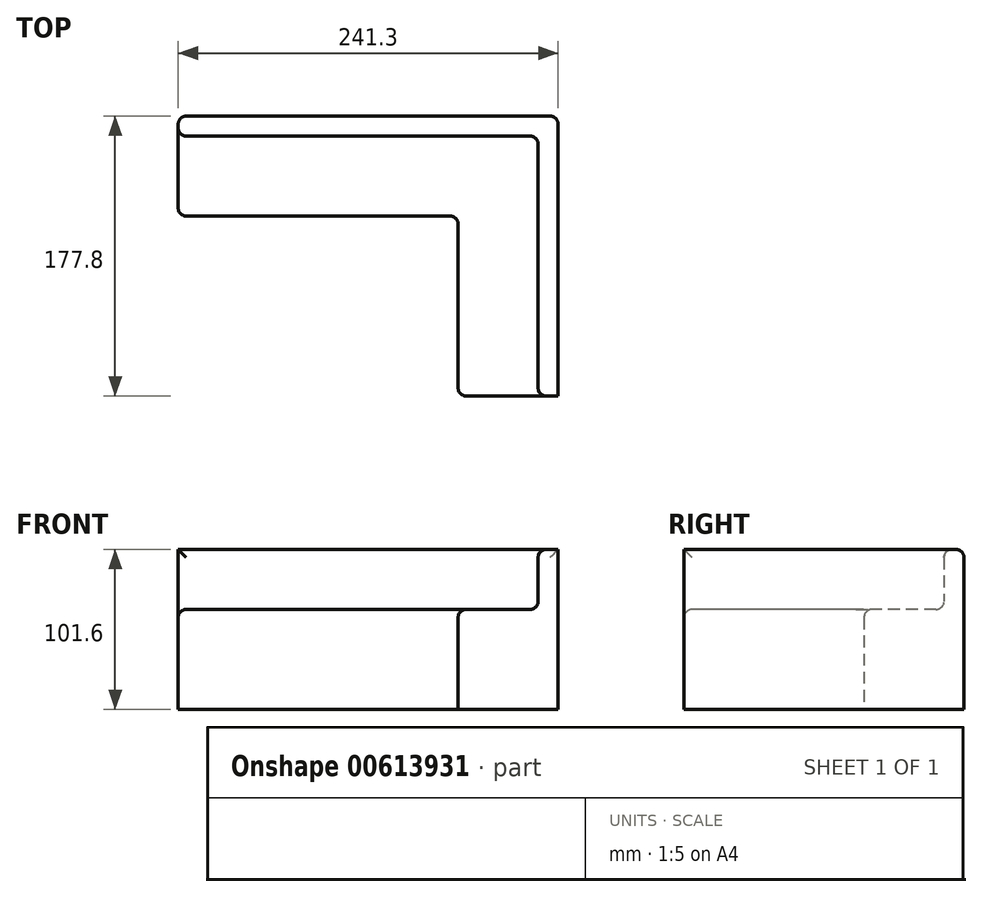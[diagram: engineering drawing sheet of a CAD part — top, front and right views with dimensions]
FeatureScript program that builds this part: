
annotation { "Feature Type Name" : "Feature", "Feature Type Description" : "" }
export const myFeature = defineFeature(function(context is Context, id is Id, definition is map)
    precondition{}
    {
        {
            var Q0;
            Q0=qCreatedBy(makeId("Top.planeOp"),FACE);
            var sketch = newSketch(context, id + "F0", { "sketchPlane" : qUnion([Q0])});
            skLineSegment(sketch, "E0.bottom", {"start": v(-200.43, 104.94) * mm, "end": v(40.87, 104.94) * mm});
            skLineSegment(sketch, "E0.top", {"start": v(-200.43, 41.44) * mm, "end": v(-22.63, 41.44) * mm});
            skLineSegment(sketch, "E0.left", {"start": v(-200.43, 104.94) * mm, "end": v(-200.43, 41.44) * mm});
            skLineSegment(sketch, "E0.right", {"start": v(40.87, 104.94) * mm, "end": v(40.87, 41.44) * mm});
            skLineSegment(sketch, "E1.top", {"start": v(-22.63, -72.86) * mm, "end": v(40.87, -72.86) * mm});
            skLineSegment(sketch, "E1.left", {"start": v(-22.63, 41.44) * mm, "end": v(-22.63, -72.86) * mm});
            skLineSegment(sketch, "E1.right", {"start": v(40.87, 41.44) * mm, "end": v(40.87, -72.86) * mm});
            skLineSegment(sketch, "E2.top", {"start": v(-200.43, 92.24) * mm, "end": v(28.17, 92.24) * mm});
            skLineSegment(sketch, "E2.left", {"start": v(-200.43, 104.94) * mm, "end": v(-200.43, 92.24) * mm});
            skLineSegment(sketch, "E2.right", {"start": v(40.87, 104.94) * mm, "end": v(40.87, 92.24) * mm});
            skLineSegment(sketch, "E3.bottom", {"start": v(28.17, 104.94) * mm, "end": v(40.87, 104.94) * mm});
            skLineSegment(sketch, "E3.top", {"start": v(28.17, -72.86) * mm, "end": v(40.87, -72.86) * mm});
            skLineSegment(sketch, "E3.left", {"start": v(28.17, 92.24) * mm, "end": v(28.17, -72.86) * mm});
            skLineSegment(sketch, "E3.right", {"start": v(40.87, 104.94) * mm, "end": v(40.87, -72.86) * mm});
            skSolve(sketch);
        }
        {
            var Q0;
            Q0=makeQuery(id+"F0.imprint","IMPRINT",FACE,{"disambiguationData":[TD([[makeQuery(id+"F0.imprint","IMPRINT",EDGE,{"derivedFrom":sQuery(id+"F0.wireOp",EDGE,"E0.bottom")}),-1.0]])]});
            extrude(context, id + "F1", {"entities" : qUnion([Q0]), "depth" : 101.6 * mm, "offsetDistance" : 25.4 * mm});
        }
        {
            var Q0;
            Q0 = qSketchRegion(id + "F0", true);
            extrude(context, id + "F2", {"entities" : qUnion([Q0]), "operationType" : NewBodyOperationType.ADD, "depth" : 63.5 * mm, "offsetDistance" : 25.4 * mm});
        }
        {
            var Q0;
            Q0=makeQuery(id+"F1.opExtrude","CAP_EDGE",EDGE,{"disambiguationData":[OSD([sQuery(id+"F0.wireOp",EDGE,"E3.left")])],"isStart":false});
            var Q1;
            Q1=makeQuery(id+"F1.opExtrude","CAP_EDGE",EDGE,{"disambiguationData":[OSD([sQuery(id+"F0.wireOp",EDGE,"E2.top")])],"isStart":false});
            var Q2;
            Q2=makeQuery(id+"F1.opExtrude","SWEPT_EDGE",EDGE,{"disambiguationData":[OSD([sQuery(id+"F0.wireOp",EDGE,"E2.top"),sQuery(id+"F0.wireOp",EDGE,"E3.left")])]});
            var Q3;
            Q3=makeQuery(id+"F2.boolean.opBoolean","INTERSECT",EDGE,{"derivedFrom":[makeQuery(id+"F1.opExtrude","SWEPT_FACE",FACE,{"disambiguationData":[OSD([sQuery(id+"F0.wireOp",EDGE,"E3.left")])]}),makeQuery(id+"F2.opExtrude","CAP_FACE",FACE,{"disambiguationData":[OSD([sQuery(id+"F0.wireOp",EDGE,"E0.top"),sQuery(id+"F0.wireOp",EDGE,"E0.left"),sQuery(id+"F0.wireOp",EDGE,"E1.top"),sQuery(id+"F0.wireOp",EDGE,"E1.left"),sQuery(id+"F0.wireOp",EDGE,"E0.bottom"),sQuery(id+"F0.wireOp",EDGE,"E2.left"),sQuery(id+"F0.wireOp",EDGE,"E3.bottom"),sQuery(id+"F0.wireOp",EDGE,"E3.top"),sQuery(id+"F0.wireOp",EDGE,"E3.right")])],"isStart":false})]});
            var Q4;
            Q4=makeQuery(id+"F1.opExtrude","SWEPT_EDGE",EDGE,{"disambiguationData":[OSD([sQuery(id+"F0.wireOp",EDGE,"E1.top"),sQuery(id+"F0.wireOp",EDGE,"E3.top"),sQuery(id+"F0.wireOp",EDGE,"E3.left")])]});
            var Q5;
            Q5=makeQuery(id+"F1.opExtrude","SWEPT_EDGE",EDGE,{"disambiguationData":[OSD([sQuery(id+"F0.wireOp",EDGE,"E0.left"),sQuery(id+"F0.wireOp",EDGE,"E2.top"),sQuery(id+"F0.wireOp",EDGE,"E2.left")])]});
            var Q6;
            Q6=makeQuery(id+"F2.boolean.opBoolean","INTERSECT",EDGE,{"derivedFrom":[makeQuery(id+"F1.opExtrude","SWEPT_FACE",FACE,{"disambiguationData":[OSD([sQuery(id+"F0.wireOp",EDGE,"E2.top")])]}),makeQuery(id+"F2.opExtrude","CAP_FACE",FACE,{"disambiguationData":[OSD([sQuery(id+"F0.wireOp",EDGE,"E0.top"),sQuery(id+"F0.wireOp",EDGE,"E0.left"),sQuery(id+"F0.wireOp",EDGE,"E1.top"),sQuery(id+"F0.wireOp",EDGE,"E1.left"),sQuery(id+"F0.wireOp",EDGE,"E0.bottom"),sQuery(id+"F0.wireOp",EDGE,"E2.left"),sQuery(id+"F0.wireOp",EDGE,"E3.bottom"),sQuery(id+"F0.wireOp",EDGE,"E3.top"),sQuery(id+"F0.wireOp",EDGE,"E3.right")])],"isStart":false})]});
            var Q7;
            Q7=makeQuery(id+"F2.opExtrude","CAP_FACE",FACE,{"disambiguationData":[OSD([sQuery(id+"F0.wireOp",EDGE,"E0.top"),sQuery(id+"F0.wireOp",EDGE,"E0.left"),sQuery(id+"F0.wireOp",EDGE,"E1.top"),sQuery(id+"F0.wireOp",EDGE,"E1.left"),sQuery(id+"F0.wireOp",EDGE,"E0.bottom"),sQuery(id+"F0.wireOp",EDGE,"E2.left"),sQuery(id+"F0.wireOp",EDGE,"E3.bottom"),sQuery(id+"F0.wireOp",EDGE,"E3.top"),sQuery(id+"F0.wireOp",EDGE,"E3.right")])],"isStart":false});
            var Q8;
            Q8=makeQuery(id+"F2.opExtrude","SWEPT_EDGE",EDGE,{"disambiguationData":[OSD([sQuery(id+"F0.wireOp",EDGE,"E0.top"),sQuery(id+"F0.wireOp",EDGE,"E1.left")])]});
            var Q9;
            Q9=makeQuery(id+"F2.opExtrude","SWEPT_EDGE",EDGE,{"disambiguationData":[OSD([sQuery(id+"F0.wireOp",EDGE,"E0.top"),sQuery(id+"F0.wireOp",EDGE,"E0.left")])]});
            var Q10;
            Q10=makeQuery(id+"F1.opExtrude","CAP_EDGE",EDGE,{"disambiguationData":[OSD([sQuery(id+"F0.wireOp",EDGE,"E0.bottom"),sQuery(id+"F0.wireOp",EDGE,"E3.bottom")])],"isStart":false});
            var Q11;
            Q11=makeQuery(id+"F1.opExtrude","CAP_EDGE",EDGE,{"disambiguationData":[OSD([sQuery(id+"F0.wireOp",EDGE,"E3.right")])],"isStart":false});
            var Q12;
            Q12=makeQuery(id+"F1.opExtrude","CAP_EDGE",EDGE,{"disambiguationData":[OSD([sQuery(id+"F0.wireOp",EDGE,"E3.top")])],"isStart":false});
            var Q13;
            Q13=makeQuery(id+"F1.opExtrude","CAP_EDGE",EDGE,{"disambiguationData":[OSD([sQuery(id+"F0.wireOp",EDGE,"E2.left")])],"isStart":false});
            var Q14;
            Q14=makeQuery(id+"F2.opExtrude","SWEPT_EDGE",EDGE,{"disambiguationData":[OSD([sQuery(id+"F0.wireOp",EDGE,"E1.top"),sQuery(id+"F0.wireOp",EDGE,"E1.left")])]});
            var Q15;
            Q15=makeQuery(id+"F1.opExtrude","SWEPT_EDGE",EDGE,{"disambiguationData":[OSD([sQuery(id+"F0.wireOp",EDGE,"E0.bottom"),sQuery(id+"F0.wireOp",EDGE,"E2.left")])]});
            var Q16;
            Q16=makeQuery(id+"F1.opExtrude","SWEPT_EDGE",EDGE,{"disambiguationData":[OSD([sQuery(id+"F0.wireOp",EDGE,"E3.top"),sQuery(id+"F0.wireOp",EDGE,"E3.right")])]});
            var Q17;
            Q17=makeQuery(id+"F1.opExtrude","SWEPT_EDGE",EDGE,{"disambiguationData":[OSD([sQuery(id+"F0.wireOp",EDGE,"E3.bottom"),sQuery(id+"F0.wireOp",EDGE,"E3.right")])]});
            fillet(context, id + "F3", {"entities" : qUnion([Q0, Q1, Q2, Q3, Q4, Q5, Q6, Q7, Q8, Q9, Q10, Q11, Q12, Q13, Q14, Q15, Q16, Q17]), "radius" : 5.08 * mm, "tangentPropagation" : true, "allowEdgeOverflow" : false});
        }
    });
